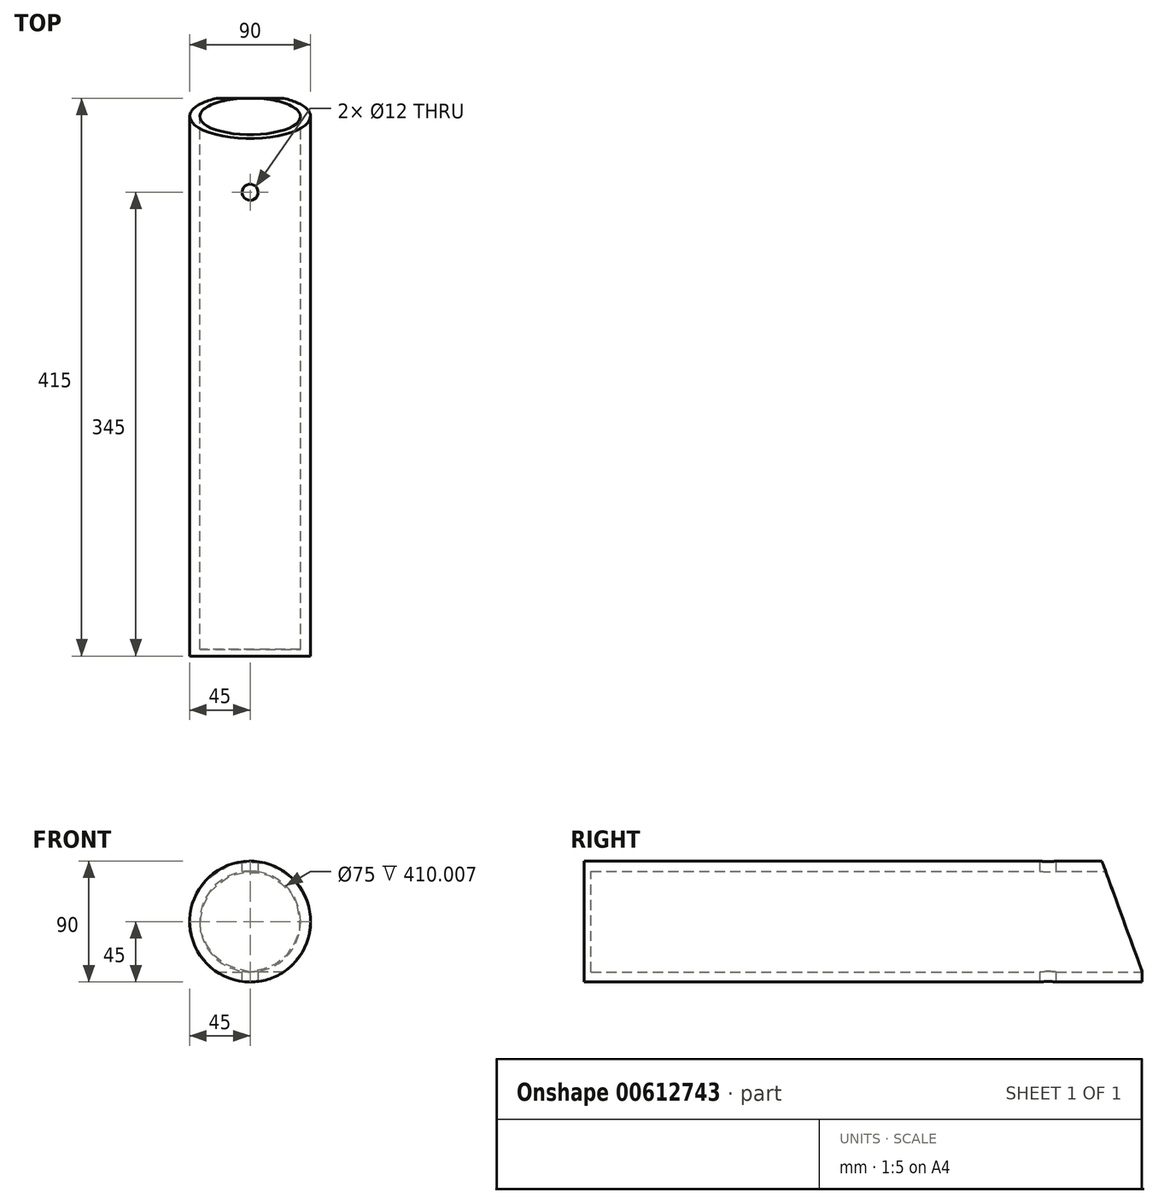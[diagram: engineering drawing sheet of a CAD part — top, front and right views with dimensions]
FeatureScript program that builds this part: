
annotation { "Feature Type Name" : "Feature", "Feature Type Description" : "" }
export const myFeature = defineFeature(function(context is Context, id is Id, definition is map)
    precondition{}
    {
        {
            var Q0;
            Q0=qCreatedBy(makeId("Front.planeOp"),FACE);
            var sketch = newSketch(context, id + "F0", { "sketchPlane" : qUnion([Q0])});
            skCircle(sketch, "E0", {"center": v(0, 0) * mm, "radius": 45 * mm});
            skCircle(sketch, "E1", {"center": v(0, 0) * mm, "radius": 37.5 * mm});
            skSolve(sketch);
        }
        {
            var Q0;
            Q0 = qSketchRegion(id + "F0", true);
            extrude(context, id + "F1", {"entities" : qUnion([Q0]), "depth" : 410 * mm, "offsetDistance" : 25 * mm});
        }
        {
            var Q0;
            Q0=qCreatedBy(makeId("Right.planeOp"),FACE);
            var sketch = newSketch(context, id + "F2", { "sketchPlane" : qUnion([Q0])});
            skLineSegment(sketch, "E2.MirrorCS", {"start": v(0, -37.5) * mm, "end": v(0, 45) * mm});
            skLineSegment(sketch, "E3.MirrorCS", {"start": v(0, 45) * mm, "end": v(-30, 45) * mm});
            skLineSegment(sketch, "E4.MirrorCS", {"start": v(0, -37.5) * mm, "end": v(-30, 45) * mm});
            skSolve(sketch);
        }
        {
            var Q0;
            Q0=makeQuery(id+"F1.opExtrude","CAP_FACE",FACE,{"disambiguationData":[OSD([sQuery(id+"F0.wireOp",EDGE,"E0"),sQuery(id+"F0.wireOp",EDGE,"E1")])],"isStart":false});
            var sketch = newSketch(context, id + "F3", { "sketchPlane" : qUnion([Q0])});
            skCircle(sketch, "E5.0", {"center": v(0, 0) * mm, "radius": 45 * mm});
            skSolve(sketch);
        }
        {
            var Q0;
            Q0 = qSketchRegion(id + "F2", true);
            extrude(context, id + "F4", {"entities" : qUnion([Q0]), "operationType" : NewBodyOperationType.REMOVE, "endBound" : BoundingType.THROUGH_ALL, "oppositeDirection" : true, "depth" : 25 * mm, "offsetDistance" : 25 * mm});
        }
        {
            var Q0;
            Q0 = qSketchRegion(id + "F2", true);
            extrude(context, id + "F5", {"entities" : qUnion([Q0]), "operationType" : NewBodyOperationType.REMOVE, "endBound" : BoundingType.THROUGH_ALL, "depth" : 25 * mm, "offsetDistance" : 25 * mm});
        }
        {
            var Q0;
            Q0 = qSketchRegion(id + "F3", true);
            extrude(context, id + "F6", {"entities" : qUnion([Q0]), "operationType" : NewBodyOperationType.ADD, "depth" : 5 * mm, "offsetDistance" : 25 * mm});
        }
        {
            var Q0;
            Q0=qCreatedBy(makeId("Top.planeOp"),FACE);
            var sketch = newSketch(context, id + "F7", { "sketchPlane" : qUnion([Q0])});
            skCircle(sketch, "E6", {"center": v(0, -70) * mm, "radius": 6 * mm});
            skSolve(sketch);
        }
        {
            var Q0;
            Q0 = qSketchRegion(id + "F7", true);
            extrude(context, id + "F8", {"entities" : qUnion([Q0]), "operationType" : NewBodyOperationType.REMOVE, "endBound" : BoundingType.SYMMETRIC, "oppositeDirection" : true, "depth" : 100 * mm, "offsetDistance" : 25 * mm});
        }
    });
